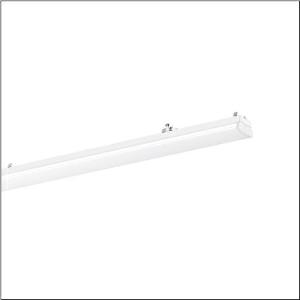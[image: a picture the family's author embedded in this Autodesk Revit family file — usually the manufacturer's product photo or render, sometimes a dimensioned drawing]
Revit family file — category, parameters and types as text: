
# Revit family: licross_r__11_recessed_opal_mo_51tl1ddn495g_fb0a
name_source: partatom
category: Lighting Fixtures
units: mm (PartAtom-declared; Revit-internal decimal feet)

## family parameters
Cut with Voids When Loaded = No
Host = Face
Light Source = No
Part Type = Normal
Room Calculation Point = No
Round Connector Dimension = Use Diameter
Shared = No

## types (1)
- --- (1 x LED, 9710 lm, 56.7 W, 4000K)
    Apparent Load = 57 VA
    CIE Flux Codes = 44 73 91 87 100
    Color Rendering = 80
    Color Temperature = 4000K
    Default Elevation = 1800 mm
    Description = Licross® 11 recessed opal MO, luminaire insert, of sheet steel, coil coated, white, length: 1.500mm, width: 76mm, height: 87mm, LED rated luminous flux: 9.710lm, light colour: 840, control gear: DALI 2, with plug, 5-pole, with phase selection, mains connection: 220..240V, AC, 50/60Hz, rated input power: 57W, halogen-free wiring, primary optical cover: cover, of PMMA, light emission: direct with ceiling illumination distribution, primary light characteristic: symmetric, protection rating (complete): IP40, insulation class (complete): insulation class I (protective earthing), certification: CE, ENEC, VDE, UKCA, protection symbol: D if used in an environment without relevant dust loads with corresponding accessories, impact resistance: IK06, permissible ambient temperature for indoor applications: -25..+35°C, corresponds to IFS (International Featured Standards) requirements for safety and quality in the food industry, reducing of maximum allowable ambient temperature of 5°C with ceiling mounting, LABS conformity tested according to VDMA 24364:2018-05, packaging unit: 1 piece
    Height = 83 mm
    Lamp = 1 x LED
    Lamp Light Flux = 9710 lm
    Lamp Power = 56.7 W
    Lamp count = 1
    Length = 1500 mm
    Luminous efficacy = 171 lm/W
    Manufacturer = Siteco
    ModVariant = No
    Model = 51TL1DDN495G
    Mounting Place = Ceiling
    Mounting Type = Pendant
    Number of Poles = 1
    OnlyDefault = Yes
    Power Factor = 1
    Product Name = Licross® 11 recessed opal MO
    Product group = luminaire insert
    ProductGroupID = 901
    Protection Class = Protection class I
    Protection Degree = IP 40
    RLX_Detail_Level = 1
    RLX_Emergency_Light_Flux = 0 lm
    RLX_Emergency_Type = 0
    RLX_Emergency_Type_DB = No
    RlxData = <blob elided: 18045 chars, md5=e659d641>
    Socket = socket
    Standby Power = 0 W
    System Light Flux = 9710 lm
    System Power = 57 W
    Type Comments = factory setting: luminous flux: 100 % | dim-lin: 254 | 378 mA
    Type Image = l_1313666.jpg
    URL = http://relux.com
    VarID = @adj_027389
    Voltage = 0 V
    Weight = 0.00 kg
    Width = 76 mm

## geometry (parser evidence)
native form markers: Blend x4, Sweep x11
no freeform markers — native parametric forms only
